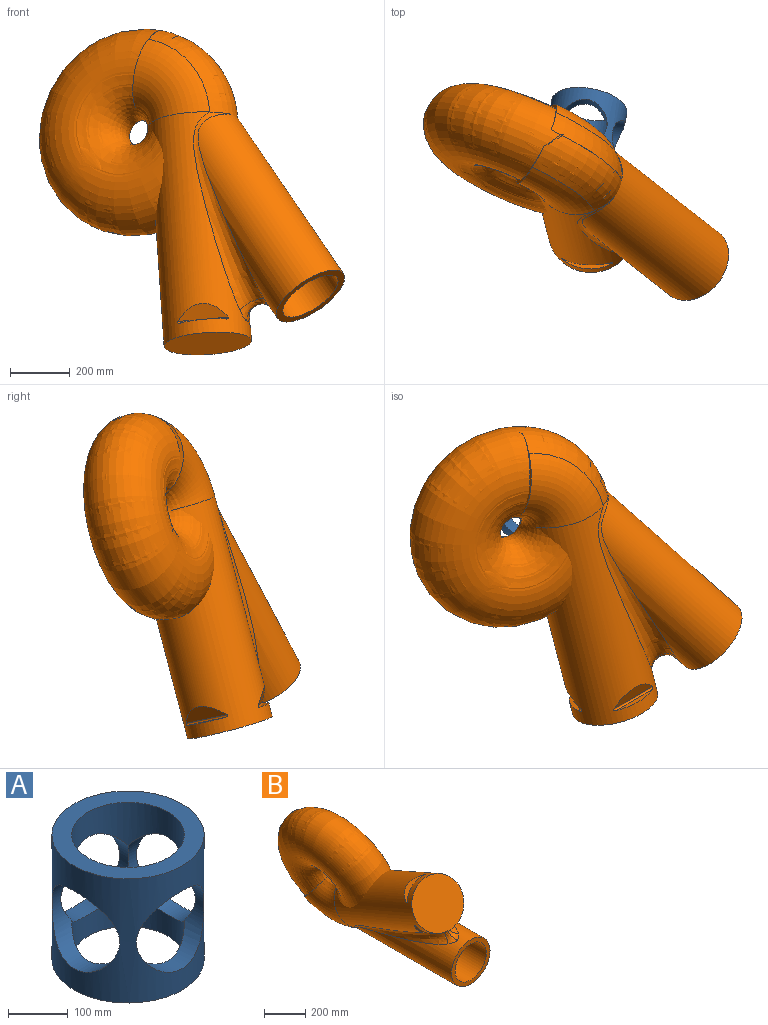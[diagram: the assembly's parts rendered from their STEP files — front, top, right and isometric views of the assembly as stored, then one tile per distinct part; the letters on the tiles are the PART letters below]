
ASSEMBLY  parts=2 mates=1
PART A: 9 faces, bbox 254.4x254.4x254 mm
  f0: cylinder r=94.12mm len=188.24mm, axis (0,0,-1), area 37300.8mm2, adj f1,f2,f3,f6,f8
  f1: cylinder r=79.49mm len=158.99mm, axis (0,-1,0), area 16406.2mm2, adj f0,f2,f4,f5,f8
  f2: cylinder r=79.49mm len=158.99mm, axis (-1,0,0), area 16405.9mm2, adj f0,f1,f3,f4,f5
  f3: cylinder r=79.49mm len=158.99mm, axis (0,1,0), area 16406.2mm2, adj f0,f2,f4,f5,f8
  f4: cylinder r=94.12mm len=188.24mm, axis (0,0,-1), area 32709.4mm2, adj f1,f2,f3,f7,f8
  f5: cylinder r=127.21mm len=254.41mm, axis (0,0,-1), area 119005.9mm2, adj f1,f2,f3,f6,f7,f8
  f6: plane 254.41x254.41mm, normal (0,0,1), area 23004.5mm2, adj f0,f5
  f7: plane 254.41x254.41mm, normal (0,0,-1), area 23004.5mm2, adj f4,f5
  f8: cylinder r=79.49mm len=158.99mm, axis (1,0,0), area 16405.1mm2, adj f0,f1,f3,f4,f5
PART B: 32 faces, bbox 494.1x1282.8x761 mm
  f0: plane 217.75x79.51mm, normal (-0.33,0.1,0.94), area 15378.1mm2, adj f1,f21,f23
  f1: cone r=133.01mm half-angle=6deg, axis (0,-1,0), area 78083.9mm2, adj f0,f17,f21,f23
  f2: bspline ~189.59x99.36mm, area 3950.7mm2, adj f3,f4,f5,f17
  f3: bspline ~189.59x107.95mm, area 3987.6mm2, adj f2,f5,f17,f20
  f4: bspline ~636.56x339.37mm, area 38001.3mm2, adj f2,f5,f17,f27
  f5: cylinder r=146.06mm len=805.98mm, axis (0.16,0.87,-0.47), area 495482.2mm2, adj f2,f3,f4,f6,f7,f8,f9,f10
  f6: plane 134.71x61.71mm, normal (0.16,0.87,-0.47), area 2532.7mm2, adj f5,f7
  f7: cylinder r=4.76mm len=148.23mm, axis (-0.85,0.37,0.38), area 1645.2mm2, adj f5,f6,f8
  f8: plane 144.93x83.7mm, normal (-0.52,-0.73,-0.45), area 6426.9mm2, adj f5,f7
  f9: plane 139.65x75.8mm, normal (0.16,0.87,-0.47), area 2532.7mm2, adj f5,f10
  f10: cylinder r=4.76mm len=153.89mm, axis (-0.01,-0.48,-0.88), area 1645.2mm2, adj f5,f9,f11
  f11: plane 150.24x90.02mm, normal (0.77,-0.56,0.29), area 6426.9mm2, adj f5,f10
  f12: plane 288.2x257.45mm, normal (-0.16,-0.87,0.47), area 67024.6mm2, adj f5
  f13: plane 136.81x78.98mm, normal (0.16,0.87,-0.47), area 2532.7mm2, adj f5,f14
  f14: cylinder r=4.76mm len=150.38mm, axis (0.86,0.11,0.5), area 1645.2mm2, adj f5,f13,f15
  f15: plane 147.89x85.67mm, normal (-0.5,-0.01,0.87), area 6426.9mm2, adj f5,f14
  f16: cylinder r=107.61mm len=656.26mm, axis (0,1,0), area 348188.9mm2, adj f18,f19
  f17: cylinder r=133.01mm len=762mm, axis (0,1,0), area 419039.8mm2, adj f1,f2,f3,f4,f18,f20,f22,f24
  f18: plane 266.02x266.02mm, normal (0,-1,0), area 19200.6mm2, adj f16,f17
  f19: cylinder r=146.06mm len=396.44mm, axis (0.16,0.87,-0.47), area 79165.7mm2, adj f16
  f20: bspline ~638.39x335.04mm, area 37947.1mm2, adj f3,f5,f17,f25
  f21: plane 201.6x121.02mm, normal (0,1,0), area 13462.5mm2, adj f0,f1
  f22: revolved ~697.42x672.77mm, area 1048876.1mm2, adj f17,f23,f27,f28
  f23: cylinder r=197.2mm len=267.17mm, axis (-0.95,0,-0.33), area 23964.5mm2, adj f0,f1,f22,f24,f28
  f24: revolved ~697.42x672.77mm, area 1048876.1mm2, adj f17,f23,f25,f28
  f25: revolved ~400.36x105.91mm, area 34426.1mm2, adj f20,f24,f26,f28
  f26: torus R=197.2mm, axis (-0.95,0,-0.33), area 132082.2mm2, adj f5,f25,f27,f28
  f27: revolved ~402.67x139.88mm, area 34425.1mm2, adj f4,f22,f26,f28
  f28: plane 285.35x232.81mm, normal (-0.21,0.76,0.62), area 35851.6mm2, adj f22,f23,f24,f25,f26,f27
  f29: plane 185.63x98.13mm, normal (0,-1,0), area 8992mm2, adj f30,f31
  f30: plane 259.08x171.58mm, normal (0.16,0.87,-0.47), area 10383.1mm2, adj f29,f31
  f31: cylinder r=107.61mm len=185.63mm, axis (0,1,0), area 0mm2, adj f29,f30
PLACE A rot(axis=(0.99,-0.14,-0.08),62deg) t=(485.8,219.97,-120.03)mm fixed
PLACE B rot(axis=(0.55,-0.79,-0.25),128.2deg) t=(498.17,403.88,-177.14)mm
MATE ball A.f0 <-> B.f5  axis (-0.16,-0.87,0.47) through (444.29,0,0)mm
